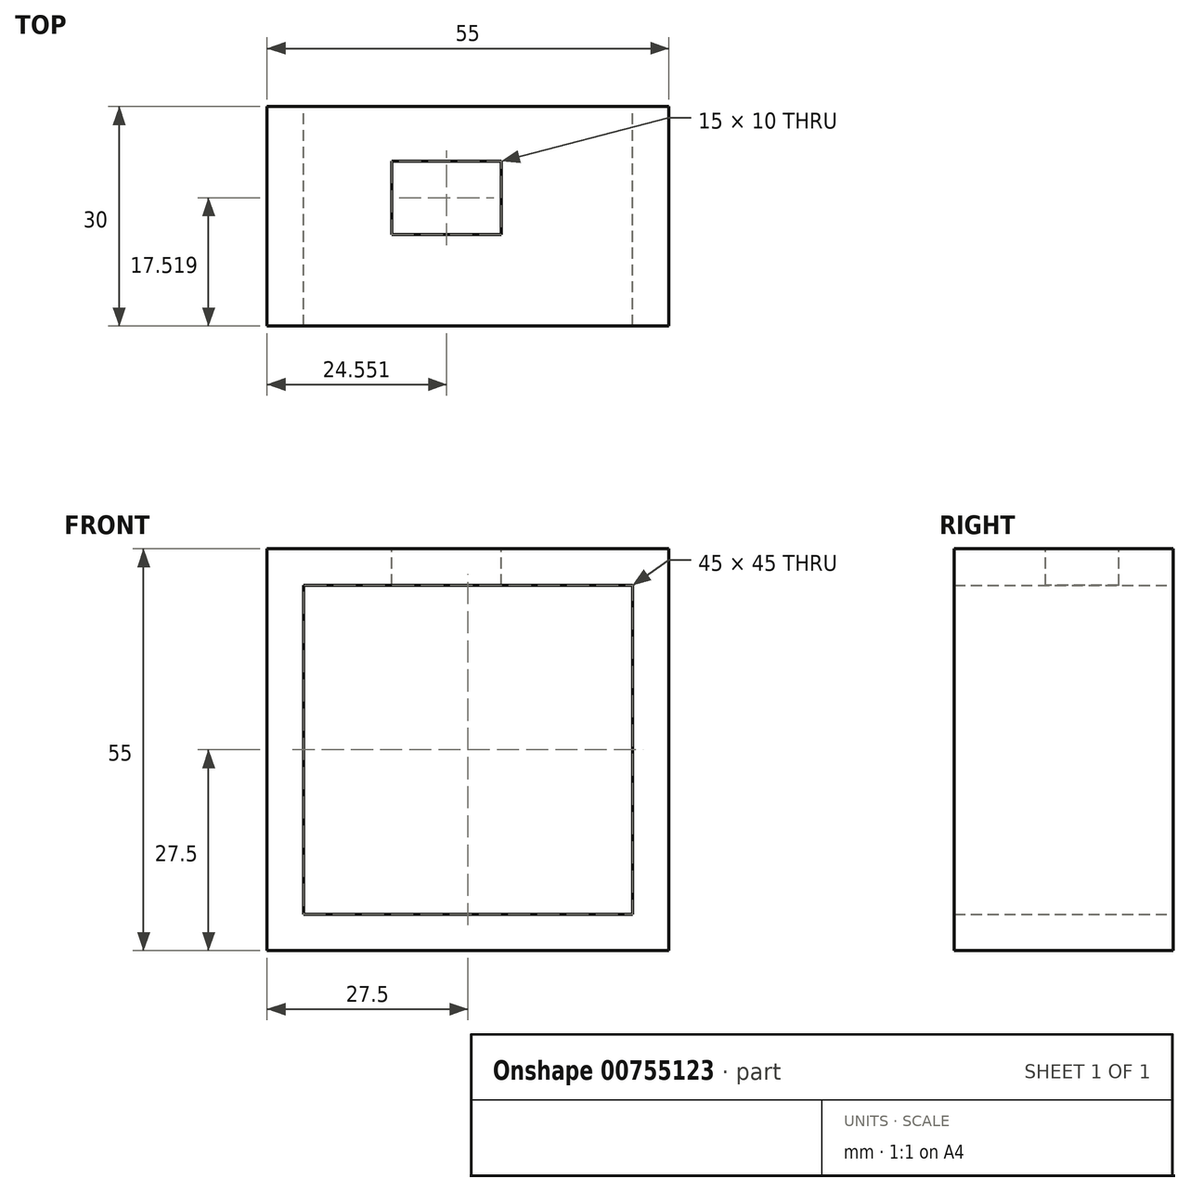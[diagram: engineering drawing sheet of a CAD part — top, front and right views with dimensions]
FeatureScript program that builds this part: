
annotation { "Feature Type Name" : "Feature", "Feature Type Description" : "" }
export const myFeature = defineFeature(function(context is Context, id is Id, definition is map)
    precondition{}
    {
        {
            var Q0;
            Q0=qCreatedBy(makeId("Front.planeOp"),FACE);
            var sketch = newSketch(context, id + "F0", { "sketchPlane" : qUnion([Q0])});
            skLineSegment(sketch, "E0.bottom", {"start": v(27.5, -27.5) * mm, "end": v(-27.5, -27.5) * mm});
            skLineSegment(sketch, "E0.top", {"start": v(27.5, 27.5) * mm, "end": v(-27.5, 27.5) * mm});
            skLineSegment(sketch, "E0.left", {"start": v(27.5, -27.5) * mm, "end": v(27.5, 27.5) * mm});
            skPoint(sketch, "E0.middle", {"position": v(0, 0) * mm});
            skLineSegment(sketch, "E1.bottom", {"start": v(22.5, -22.5) * mm, "end": v(-22.5, -22.5) * mm});
            skLineSegment(sketch, "E1.top", {"start": v(22.5, 22.5) * mm, "end": v(-22.5, 22.5) * mm});
            skLineSegment(sketch, "E1.left", {"start": v(22.5, -22.5) * mm, "end": v(22.5, 22.5) * mm});
            skLineSegment(sketch, "E1.right", {"start": v(-22.5, -22.5) * mm, "end": v(-22.5, 22.5) * mm});
            skLineSegment(sketch, "E2", {"start": v(-27.5, 27.5) * mm, "end": v(-27.5, -27.5) * mm});
            skSolve(sketch);
        }
        {
            var Q0;
            Q0=makeQuery(id+"F0.imprint","IMPRINT",FACE,{"disambiguationData":[TD([[makeQuery(id+"F0.imprint","IMPRINT",EDGE,{"derivedFrom":sQuery(id+"F0.wireOp",EDGE,"E0.bottom")}),-1.0]])]});
            var Q1;
            Q1=makeQuery(id+"F0.imprint","IMPRINT",FACE,{"disambiguationData":[TD([[makeQuery(id+"F0.imprint","IMPRINT",EDGE,{"derivedFrom":sQuery(id+"F0.wireOp",EDGE,"E0.right")}),1.0]])]});
            var Q2;
            Q2=makeQuery(id+"F0.imprint","IMPRINT",FACE,{"disambiguationData":[TD([[makeQuery(id+"F0.imprint","IMPRINT",EDGE,{"derivedFrom":sQuery(id+"F0.wireOp",EDGE,"E0.left")}),-1.0]])]});
            extrude(context, id + "F1", {"entities" : qUnion([Q0, Q1, Q2]), "depth" : 30 * mm, "offsetDistance" : 25 * mm});
        }
        {
            var Q0;
            Q0=makeQuery(id+"F1.opExtrude","SWEPT_FACE",FACE,{"disambiguationData":[OSD([sQuery(id+"F0.wireOp",EDGE,"E0.top")])]});
            var sketch = newSketch(context, id + "F2", { "sketchPlane" : qUnion([Q0])});
            skLineSegment(sketch, "E3.bottom", {"start": v(4.55, -17.48) * mm, "end": v(-10.45, -17.48) * mm});
            skLineSegment(sketch, "E3.top", {"start": v(4.55, -7.48) * mm, "end": v(-10.45, -7.48) * mm});
            skLineSegment(sketch, "E3.left", {"start": v(4.55, -17.48) * mm, "end": v(4.55, -7.48) * mm});
            skLineSegment(sketch, "E3.right", {"start": v(-10.45, -17.48) * mm, "end": v(-10.45, -7.48) * mm});
            skPoint(sketch, "E3.middle", {"position": v(-2.95, -12.48) * mm});
            skSolve(sketch);
        }
        {
            var Q0;
            Q0=makeQuery(id+"F2.imprint","IMPRINT",FACE,{"disambiguationData":[TD([[makeQuery(id+"F2.imprint","IMPRINT",EDGE,{"derivedFrom":sQuery(id+"F2.wireOp",EDGE,"E3.bottom")}),-1.0]])]});
            extrude(context, id + "F3", {"entities" : qUnion([Q0]), "operationType" : NewBodyOperationType.REMOVE, "oppositeDirection" : true, "depth" : 25 * mm, "offsetDistance" : 25 * mm});
        }
    });
